# Revit family: Ottoman-Soft_Seating-Allermuir-Pebble
name_source: partatom
category: Furniture
revit_build: Autodesk Revit Architecture 2012 (Build: 20110309_2315(x64)
units: mm (PartAtom-declared; Revit-internal decimal feet)

## types (3) — shared parameters
04 CSI = 12 51 00
95 CSI = 12510
Assembly Code = E2020200
Brochure URL = http://www.allermuir.net
CAD Blocks URL = http://www.allermuir.net
Color Availability = See price list for material options
Fabric Spec Sheets = http://www.allermuir.net
Glide Finish = Laminate - Allermuir - Clear
LEED Stats URL = http://www.allermuir.net
Leg Support Finish = Metal - Allermuir - Silver
Manufacturer = Allermuir
Manufacturer Fax = (419) 887 5805
Overall Height = 1' - 5"
Overall Width = 2' - 4 3/4"
Plugin Data URL = http://products.ecoscorecard.com
Pricing URL = http://www.allermuir.net
Product Line = Pebble
Product Page URL = http://www.allermuir.net
Seat Finish = Fabric - Allermuir - Silcoates
Specifications URL = http://www.allermuir.net
Stacks = No
Subcategory = Soft Seating
URL = http://www.allermuir.net
Weight = 25.0 lb
White Plastic Back Membrane = No
ecoScorecard Product Page = http://products.ecoscorecard.com
ecoScorecard_data = http://thesenatorgroup.ecoscorecard.com

## per-type parameters (varying)
| type | Description | Model | Seat | Seat Top Finish |
| A620 - Pebble | Pebble | A620 | Pebble : A620 - Pebble | <By Category> |
| A621 - Pebble Scallop | Pebble Scallop | A621 | Pebble : A621 - Pebble Scallop | <By Category> |
| A622 - Pebble Table | Pebble table | A622 | Pebble : A622 - Pebble Table | Fabric - Allermuir - Upholstery - Pebbled - Light Brown |

## geometry (parser evidence)
native form markers: Blend x9, Sweep x8
no freeform markers — native parametric forms only
